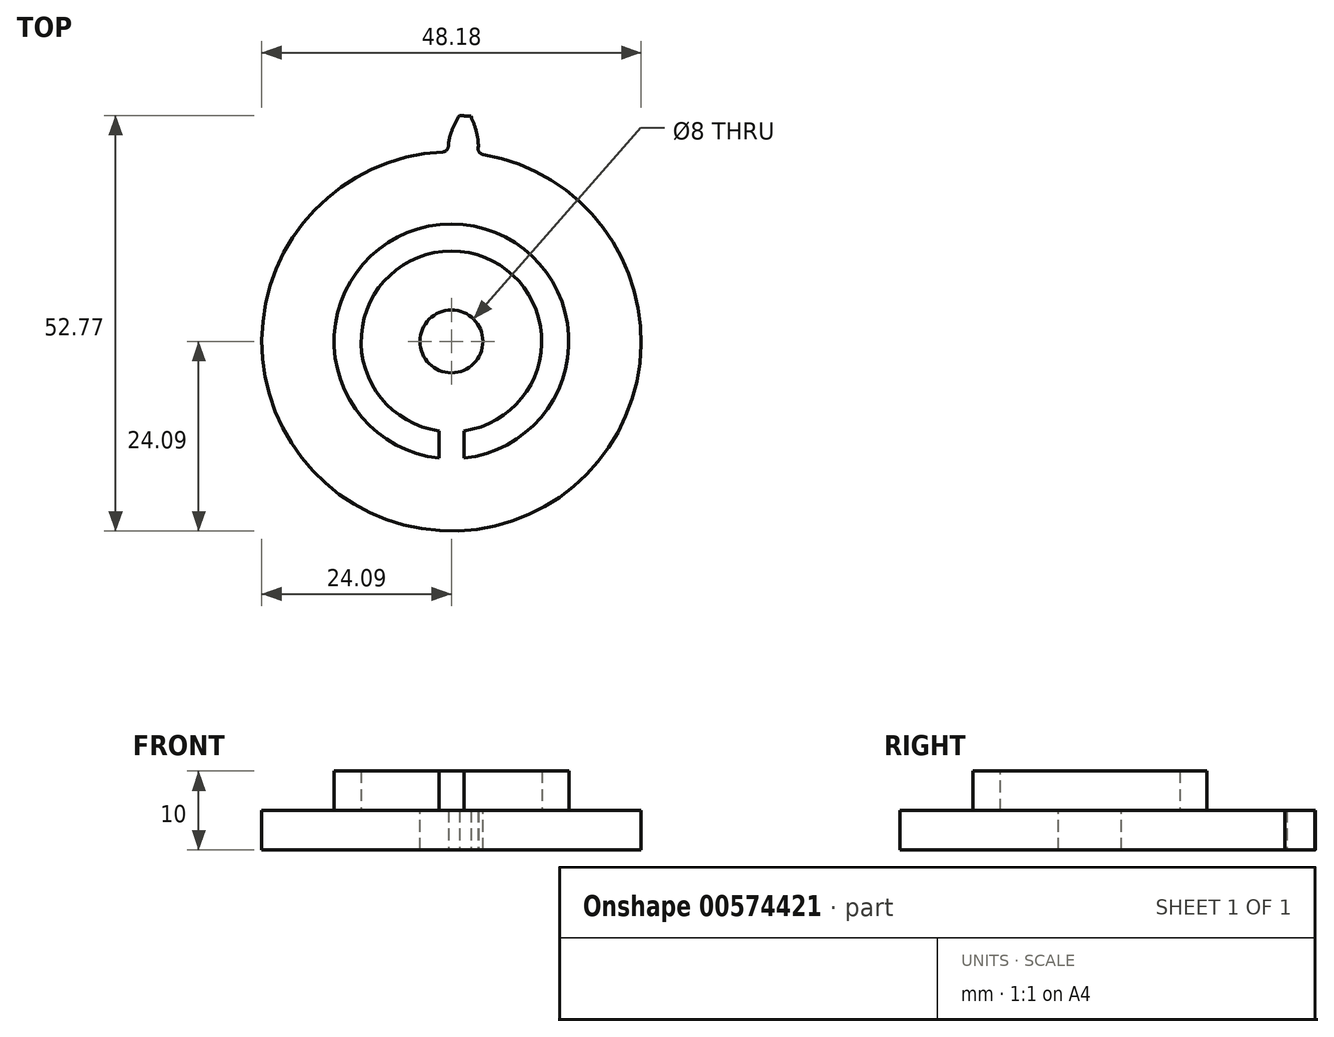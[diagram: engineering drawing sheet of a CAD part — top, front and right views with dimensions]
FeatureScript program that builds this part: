
annotation { "Feature Type Name" : "Feature", "Feature Type Description" : "" }
export const myFeature = defineFeature(function(context is Context, id is Id, definition is map)
    precondition{}
    {
        {
            var Q0;
            Q0=qCreatedBy(makeId("Front.planeOp"),FACE);
            var sketch = newSketch(context, id + "F0", { "sketchPlane" : qUnion([Q0])});
            skLineSegment(sketch, "E0", {"start": v(0, 72.27) * mm, "end": v(0, -50.25) * mm, "construction": true});
            skSolve(sketch);
        }
        {
            var Q0;
            Q0=qCreatedBy(makeId("Top.planeOp"),FACE);
            var sketch = newSketch(context, id + "F1", { "sketchPlane" : qUnion([Q0])});
            skCircle(sketch, "E1", {"center": v(0, 0) * mm, "radius": 26.65 * mm, "construction": true});
            skCircle(sketch, "E2", {"center": v(0, 0) * mm, "radius": 24.09 * mm});
            skSolve(sketch);
        }
        {
            var Q0;
            Q0=qSketchRegion(id+"F1",true);
            extrude(context, id + "F2", {"entities" : qUnion([Q0]), "depth" : 5 * mm});
        }
        {
            var Q0;
            Q0=makeQuery(id+"F2.opExtrude","CAP_FACE",FACE,{"disambiguationData":[OSD([sQuery(id+"F1.wireOp",EDGE,"E2"),sQuery(id+"F1.wireOp",EDGE,"lKhcHiEn-qWT4-b5GR-9CCX-N4hY3lJjeW35"),sQuery(id+"F1.wireOp",EDGE,"zsuhm7zz-1LAn-hH0Z-Fbhr-HMJ1RvOiH2OX")])],"isStart":false});
            var sketch = newSketch(context, id + "F3", { "sketchPlane" : qUnion([Q0])});
            skArc(sketch, "E3", {"start": v(-2.86, 2.8) * mm, "mid": v(0, -4) * mm, "end": v(2.86, 2.8) * mm});
            skPoint(sketch, "E4", {"position": v(0, 4) * mm});
            skArc(sketch, "E5", {"start": v(-2.86, 2.8) * mm, "mid": v(0, 4) * mm, "end": v(2.86, 2.8) * mm, "construction": true});
            skArc(sketch, "E6", {"start": v(-2.86, 2.8) * mm, "mid": v(1.55, -3.69) * mm, "end": v(0, 4) * mm});
            skArc(sketch, "E7", {"start": v(0, 4) * mm, "mid": v(-2.83, 2.83) * mm, "end": v(-4, 0) * mm});
            skSolve(sketch);
        }
        {
            var Q0;
            Q0=qSketchRegion(id+"F3",true);
            extrude(context, id + "F4", {"entities" : qUnion([Q0]), "operationType" : NewBodyOperationType.REMOVE, "endBound" : BoundingType.THROUGH_ALL, "oppositeDirection" : true, "depth" : 25 * mm});
        }
        {
            var Q0;
            Q0=qCreatedBy(makeId("Top.planeOp"),FACE);
            var sketch = newSketch(context, id + "F5", { "sketchPlane" : qUnion([Q0])});
            skLineSegment(sketch, "E8", {"start": v(0, 0) * mm, "end": v(0, 29.7) * mm, "construction": true});
            skLineSegment(sketch, "E9", {"start": v(0, 0) * mm, "end": v(-10.47, 28.76) * mm, "construction": true});
            skLineSegment(sketch, "E10", {"start": v(0, 26.65) * mm, "end": v(-8.57, 23.53) * mm, "construction": true});
            skCircle(sketch, "E11", {"center": v(0, 0) * mm, "radius": 26.65 * mm, "construction": true});
            skCircle(sketch, "E12", {"center": v(0, 0) * mm, "radius": 28.7 * mm, "construction": true});
            skArc(sketch, "E13", {"start": v(-1.13, 24.06) * mm, "mid": v(-1.46, -24.04) * mm, "end": v(4.02, 23.75) * mm, "construction": true});
            skCircle(sketch, "E14", {"center": v(0, 0) * mm, "radius": 25.04 * mm, "construction": true});
            skCircle(sketch, "E15", {"center": v(11, 22.5) * mm, "radius": 11.76 * mm, "construction": true});
            skCircle(sketch, "E16", {"center": v(6.53, 24.18) * mm, "radius": 6.98 * mm, "construction": true});
            skArc(sketch, "E17", {"start": v(1, 28.68) * mm, "mid": v(0.45, 27.7) * mm, "end": v(0, 26.65) * mm});
            skArc(sketch, "E18", {"start": v(0, 26.65) * mm, "mid": v(-0.25, 25.86) * mm, "end": v(-0.4, 25.04) * mm});
            skLineSegment(sketch, "E19", {"start": v(-0.4, 25.04) * mm, "end": v(-0.4, 24.84) * mm});
            skLineSegment(sketch, "E20", {"start": v(-0.38, 24.08) * mm, "end": v(0, 0) * mm, "construction": true});
            skArc(sketch, "E21", {"start": v(3.21, 26.46) * mm, "mid": v(1.61, 26.6) * mm, "end": v(0, 26.65) * mm});
            skLineSegment(sketch, "E22", {"start": v(0, 0) * mm, "end": v(1.61, 26.6) * mm, "construction": true});
            skLineSegment(sketch, "E23", {"start": v(0.78, 12.85) * mm, "end": v(1.61, 26.6) * mm, "construction": true});
            skArc(sketch, "E24", {"start": v(1.73, 28.65) * mm, "mid": v(1.37, 28.67) * mm, "end": v(1, 28.68) * mm});
            skArc(sketch, "E25.MirrorCS", {"start": v(1.73, 28.65) * mm, "mid": v(2.1, 28.62) * mm, "end": v(2.47, 28.6) * mm});
            skArc(sketch, "E26.MirrorCS", {"start": v(2.47, 28.6) * mm, "mid": v(2.9, 27.54) * mm, "end": v(3.21, 26.46) * mm});
            skArc(sketch, "E27.MirrorCS", {"start": v(3.21, 26.46) * mm, "mid": v(3.36, 25.64) * mm, "end": v(3.42, 24.8) * mm});
            skLineSegment(sketch, "E28.MirrorCS", {"start": v(3.42, 24.8) * mm, "end": v(3.39, 24.61) * mm});
            skPoint(sketch, "E29.visualSharp", {"position": v(-0.38, 24.08) * mm});
            skArc(sketch, "E29.filletArc", {"start": v(-1.13, 24.06) * mm, "mid": v(-0.6, 24.3) * mm, "end": v(-0.4, 24.84) * mm});
            skArc(sketch, "E30.MirrorCS", {"start": v(4.02, 23.75) * mm, "mid": v(3.53, 24.05) * mm, "end": v(3.39, 24.61) * mm});
            skPoint(sketch, "E31.orphan", {"position": v(3.29, 23.86) * mm});
            skArc(sketch, "E32", {"start": v(-1.13, 24.06) * mm, "mid": v(1.46, 24.04) * mm, "end": v(4.02, 23.75) * mm});
            skSolve(sketch);
        }
        {
            var Q0;
            Q0=qSketchRegion(id+"F5",true);
            extrude(context, id + "F6", {"entities" : qUnion([Q0]), "operationType" : NewBodyOperationType.ADD, "depth" : 5 * mm});
        }
        {
            var Q0;
            {var subQ0=sQuery(id+"F5.wireOp",EDGE,"E32");var subQ1=sQuery(id+"F5.wireOp",EDGE,"E30.MirrorCS");var subQ2=sQuery(id+"F5.wireOp",EDGE,"E29.filletArc");var subQ3=sQuery(id+"F5.wireOp",EDGE,"E28.MirrorCS");var subQ4=sQuery(id+"F5.wireOp",EDGE,"E27.MirrorCS");var subQ5=sQuery(id+"F5.wireOp",EDGE,"E26.MirrorCS");var subQ6=sQuery(id+"F5.wireOp",EDGE,"E25.MirrorCS");var subQ7=sQuery(id+"F5.wireOp",EDGE,"E24");var subQ8=sQuery(id+"F5.wireOp",EDGE,"E19");var subQ9=sQuery(id+"F5.wireOp",EDGE,"E18");var subQ10=sQuery(id+"F5.wireOp",EDGE,"E17");Q0=makeQuery(id+"FKo0gFQ4KOUnKrD_1.25.F6.boolean.opBoolean","MERGE",FACE,{"derivedFrom":[makeQuery(id+"FKo0gFQ4KOUnKrD_1.24.F6.boolean.opBoolean","MERGE",FACE,{"derivedFrom":[makeQuery(id+"FKo0gFQ4KOUnKrD_1.23.F6.boolean.opBoolean","MERGE",FACE,{"derivedFrom":[makeQuery(id+"FKo0gFQ4KOUnKrD_1.22.F6.boolean.opBoolean","MERGE",FACE,{"derivedFrom":[makeQuery(id+"FKo0gFQ4KOUnKrD_1.21.F6.boolean.opBoolean","MERGE",FACE,{"derivedFrom":[makeQuery(id+"FKo0gFQ4KOUnKrD_1.20.F6.boolean.opBoolean","MERGE",FACE,{"derivedFrom":[makeQuery(id+"FKo0gFQ4KOUnKrD_1.19.F6.boolean.opBoolean","MERGE",FACE,{"derivedFrom":[makeQuery(id+"FKo0gFQ4KOUnKrD_1.18.F6.boolean.opBoolean","MERGE",FACE,{"derivedFrom":[makeQuery(id+"FKo0gFQ4KOUnKrD_1.17.F6.boolean.opBoolean","MERGE",FACE,{"derivedFrom":[makeQuery(id+"FKo0gFQ4KOUnKrD_1.16.F6.boolean.opBoolean","MERGE",FACE,{"derivedFrom":[makeQuery(id+"FKo0gFQ4KOUnKrD_1.15.F6.boolean.opBoolean","MERGE",FACE,{"derivedFrom":[makeQuery(id+"FKo0gFQ4KOUnKrD_1.14.F6.boolean.opBoolean","MERGE",FACE,{"derivedFrom":[makeQuery(id+"FKo0gFQ4KOUnKrD_1.13.F6.boolean.opBoolean","MERGE",FACE,{"derivedFrom":[makeQuery(id+"FKo0gFQ4KOUnKrD_1.12.F6.boolean.opBoolean","MERGE",FACE,{"derivedFrom":[makeQuery(id+"FKo0gFQ4KOUnKrD_1.11.F6.boolean.opBoolean","MERGE",FACE,{"derivedFrom":[makeQuery(id+"FKo0gFQ4KOUnKrD_1.10.F6.boolean.opBoolean","MERGE",FACE,{"derivedFrom":[makeQuery(id+"FKo0gFQ4KOUnKrD_1.9.F6.boolean.opBoolean","MERGE",FACE,{"derivedFrom":[makeQuery(id+"FKo0gFQ4KOUnKrD_1.8.F6.boolean.opBoolean","MERGE",FACE,{"derivedFrom":[makeQuery(id+"FKo0gFQ4KOUnKrD_1.7.F6.boolean.opBoolean","MERGE",FACE,{"derivedFrom":[makeQuery(id+"FKo0gFQ4KOUnKrD_1.6.F6.boolean.opBoolean","MERGE",FACE,{"derivedFrom":[makeQuery(id+"FKo0gFQ4KOUnKrD_1.5.F6.boolean.opBoolean","MERGE",FACE,{"derivedFrom":[makeQuery(id+"FKo0gFQ4KOUnKrD_1.4.F6.boolean.opBoolean","MERGE",FACE,{"derivedFrom":[makeQuery(id+"FKo0gFQ4KOUnKrD_1.3.F6.boolean.opBoolean","MERGE",FACE,{"derivedFrom":[makeQuery(id+"FKo0gFQ4KOUnKrD_1.2.F6.boolean.opBoolean","MERGE",FACE,{"derivedFrom":[makeQuery(id+"FKo0gFQ4KOUnKrD_1.1.F6.boolean.opBoolean","MERGE",FACE,{"derivedFrom":[makeQuery(id+"F6.boolean.opBoolean","MERGE",FACE,{"derivedFrom":[makeQuery(id+"F2.opExtrude","CAP_FACE",FACE,{"disambiguationData":[OSD([sQuery(id+"F1.wireOp",EDGE,"E2")])],"isStart":false}),makeQuery(id+"F6.opExtrude","CAP_FACE",FACE,{"disambiguationData":[OSD([subQ10,subQ9,subQ8,subQ7,subQ6,subQ5,subQ4,subQ3,subQ2,subQ1,subQ0])],"isStart":false})]}),makeQuery(id+"FKo0gFQ4KOUnKrD_1.1.F6.opExtrude","CAP_FACE",FACE,{"disambiguationData":[OSD([subQ10,subQ9,subQ8,subQ7,subQ6,subQ5,subQ4,subQ3,subQ2,subQ1,subQ0])],"isStart":false})]}),makeQuery(id+"FKo0gFQ4KOUnKrD_1.2.F6.opExtrude","CAP_FACE",FACE,{"disambiguationData":[OSD([subQ10,subQ9,subQ8,subQ7,subQ6,subQ5,subQ4,subQ3,subQ2,subQ1,subQ0])],"isStart":false})]}),makeQuery(id+"FKo0gFQ4KOUnKrD_1.3.F6.opExtrude","CAP_FACE",FACE,{"disambiguationData":[OSD([subQ10,subQ9,subQ8,subQ7,subQ6,subQ5,subQ4,subQ3,subQ2,subQ1,subQ0])],"isStart":false})]}),makeQuery(id+"FKo0gFQ4KOUnKrD_1.4.F6.opExtrude","CAP_FACE",FACE,{"disambiguationData":[OSD([subQ10,subQ9,subQ8,subQ7,subQ6,subQ5,subQ4,subQ3,subQ2,subQ1,subQ0])],"isStart":false})]}),makeQuery(id+"FKo0gFQ4KOUnKrD_1.5.F6.opExtrude","CAP_FACE",FACE,{"disambiguationData":[OSD([subQ10,subQ9,subQ8,subQ7,subQ6,subQ5,subQ4,subQ3,subQ2,subQ1,subQ0])],"isStart":false})]}),makeQuery(id+"FKo0gFQ4KOUnKrD_1.6.F6.opExtrude","CAP_FACE",FACE,{"disambiguationData":[OSD([subQ10,subQ9,subQ8,subQ7,subQ6,subQ5,subQ4,subQ3,subQ2,subQ1,subQ0])],"isStart":false})]}),makeQuery(id+"FKo0gFQ4KOUnKrD_1.7.F6.opExtrude","CAP_FACE",FACE,{"disambiguationData":[OSD([subQ10,subQ9,subQ8,subQ7,subQ6,subQ5,subQ4,subQ3,subQ2,subQ1,subQ0])],"isStart":false})]}),makeQuery(id+"FKo0gFQ4KOUnKrD_1.8.F6.opExtrude","CAP_FACE",FACE,{"disambiguationData":[OSD([subQ10,subQ9,subQ8,subQ7,subQ6,subQ5,subQ4,subQ3,subQ2,subQ1,subQ0])],"isStart":false})]}),makeQuery(id+"FKo0gFQ4KOUnKrD_1.9.F6.opExtrude","CAP_FACE",FACE,{"disambiguationData":[OSD([subQ10,subQ9,subQ8,subQ7,subQ6,subQ5,subQ4,subQ3,subQ2,subQ1,subQ0])],"isStart":false})]}),makeQuery(id+"FKo0gFQ4KOUnKrD_1.10.F6.opExtrude","CAP_FACE",FACE,{"disambiguationData":[OSD([subQ10,subQ9,subQ8,subQ7,subQ6,subQ5,subQ4,subQ3,subQ2,subQ1,subQ0])],"isStart":false})]}),makeQuery(id+"FKo0gFQ4KOUnKrD_1.11.F6.opExtrude","CAP_FACE",FACE,{"disambiguationData":[OSD([subQ10,subQ9,subQ8,subQ7,subQ6,subQ5,subQ4,subQ3,subQ2,subQ1,subQ0])],"isStart":false})]}),makeQuery(id+"FKo0gFQ4KOUnKrD_1.12.F6.opExtrude","CAP_FACE",FACE,{"disambiguationData":[OSD([subQ10,subQ9,subQ8,subQ7,subQ6,subQ5,subQ4,subQ3,subQ2,subQ1,subQ0])],"isStart":false})]}),makeQuery(id+"FKo0gFQ4KOUnKrD_1.13.F6.opExtrude","CAP_FACE",FACE,{"disambiguationData":[OSD([subQ10,subQ9,subQ8,subQ7,subQ6,subQ5,subQ4,subQ3,subQ2,subQ1,subQ0])],"isStart":false})]}),makeQuery(id+"FKo0gFQ4KOUnKrD_1.14.F6.opExtrude","CAP_FACE",FACE,{"disambiguationData":[OSD([subQ10,subQ9,subQ8,subQ7,subQ6,subQ5,subQ4,subQ3,subQ2,subQ1,subQ0])],"isStart":false})]}),makeQuery(id+"FKo0gFQ4KOUnKrD_1.15.F6.opExtrude","CAP_FACE",FACE,{"disambiguationData":[OSD([subQ10,subQ9,subQ8,subQ7,subQ6,subQ5,subQ4,subQ3,subQ2,subQ1,subQ0])],"isStart":false})]}),makeQuery(id+"FKo0gFQ4KOUnKrD_1.16.F6.opExtrude","CAP_FACE",FACE,{"disambiguationData":[OSD([subQ10,subQ9,subQ8,subQ7,subQ6,subQ5,subQ4,subQ3,subQ2,subQ1,subQ0])],"isStart":false})]}),makeQuery(id+"FKo0gFQ4KOUnKrD_1.17.F6.opExtrude","CAP_FACE",FACE,{"disambiguationData":[OSD([subQ10,subQ9,subQ8,subQ7,subQ6,subQ5,subQ4,subQ3,subQ2,subQ1,subQ0])],"isStart":false})]}),makeQuery(id+"FKo0gFQ4KOUnKrD_1.18.F6.opExtrude","CAP_FACE",FACE,{"disambiguationData":[OSD([subQ10,subQ9,subQ8,subQ7,subQ6,subQ5,subQ4,subQ3,subQ2,subQ1,subQ0])],"isStart":false})]}),makeQuery(id+"FKo0gFQ4KOUnKrD_1.19.F6.opExtrude","CAP_FACE",FACE,{"disambiguationData":[OSD([subQ10,subQ9,subQ8,subQ7,subQ6,subQ5,subQ4,subQ3,subQ2,subQ1,subQ0])],"isStart":false})]}),makeQuery(id+"FKo0gFQ4KOUnKrD_1.20.F6.opExtrude","CAP_FACE",FACE,{"disambiguationData":[OSD([subQ10,subQ9,subQ8,subQ7,subQ6,subQ5,subQ4,subQ3,subQ2,subQ1,subQ0])],"isStart":false})]}),makeQuery(id+"FKo0gFQ4KOUnKrD_1.21.F6.opExtrude","CAP_FACE",FACE,{"disambiguationData":[OSD([subQ10,subQ9,subQ8,subQ7,subQ6,subQ5,subQ4,subQ3,subQ2,subQ1,subQ0])],"isStart":false})]}),makeQuery(id+"FKo0gFQ4KOUnKrD_1.22.F6.opExtrude","CAP_FACE",FACE,{"disambiguationData":[OSD([subQ10,subQ9,subQ8,subQ7,subQ6,subQ5,subQ4,subQ3,subQ2,subQ1,subQ0])],"isStart":false})]}),makeQuery(id+"FKo0gFQ4KOUnKrD_1.23.F6.opExtrude","CAP_FACE",FACE,{"disambiguationData":[OSD([subQ10,subQ9,subQ8,subQ7,subQ6,subQ5,subQ4,subQ3,subQ2,subQ1,subQ0])],"isStart":false})]}),makeQuery(id+"FKo0gFQ4KOUnKrD_1.24.F6.opExtrude","CAP_FACE",FACE,{"disambiguationData":[OSD([subQ10,subQ9,subQ8,subQ7,subQ6,subQ5,subQ4,subQ3,subQ2,subQ1,subQ0])],"isStart":false})]}),makeQuery(id+"FKo0gFQ4KOUnKrD_1.25.F6.opExtrude","CAP_FACE",FACE,{"disambiguationData":[OSD([subQ10,subQ9,subQ8,subQ7,subQ6,subQ5,subQ4,subQ3,subQ2,subQ1,subQ0])],"isStart":false})]});}
            var sketch = newSketch(context, id + "F7", { "sketchPlane" : qUnion([Q0])});
            skCircle(sketch, "E33", {"center": v(0, 0) * mm, "radius": 11.48 * mm});
            skCircle(sketch, "E34", {"center": v(0, 0) * mm, "radius": 14.9 * mm});
            skSolve(sketch);
        }
        {
            var Q0;
            Q0=makeQuery(id+"F7.imprint","IMPRINT",FACE,{"disambiguationData":[TD([[makeQuery(id+"F7.imprint","IMPRINT",EDGE,{"derivedFrom":sQuery(id+"F7.wireOp",EDGE,"E33")}),-1.0]])]});
            extrude(context, id + "F8", {"entities" : qUnion([Q0]), "operationType" : NewBodyOperationType.ADD, "depth" : 5 * mm});
        }
        {
            var Q0;
            Q0=makeQuery(id+"F8.opExtrude","CAP_FACE",FACE,{"disambiguationData":[OSD([sQuery(id+"F7.wireOp",EDGE,"E33"),sQuery(id+"F7.wireOp",EDGE,"E34")])],"isStart":false});
            var sketch = newSketch(context, id + "F9", { "sketchPlane" : qUnion([Q0])});
            skLineSegment(sketch, "E35", {"start": v(0, -11.48) * mm, "end": v(0, -14.9) * mm});
            skLineSegment(sketch, "E36", {"start": v(1.6, -11.36) * mm, "end": v(1.6, -14.82) * mm});
            skLineSegment(sketch, "E37", {"start": v(1.6, -13.1) * mm, "end": v(0, -13.1) * mm});
            skLineSegment(sketch, "E38", {"start": v(0, -13.1) * mm, "end": v(-1.6, -13.1) * mm});
            skLineSegment(sketch, "E39", {"start": v(-1.6, -13.1) * mm, "end": v(-1.6, -11.36) * mm});
            skLineSegment(sketch, "E40", {"start": v(-1.6, -13.1) * mm, "end": v(-1.6, -14.82) * mm});
            skSolve(sketch);
        }
        {
            var Q0;
            {var subQ3=sQuery(id+"F9.wireOp",EDGE,"E37");Q0=makeQuery(id+"F9.imprint","IMPRINT",FACE,{"disambiguationData":[TD([[makeQuery(id+"F9.imprint","IMPRINT",EDGE,{"derivedFrom":subQ3}),1.0]])]});}
            var Q1;
            {var subQ3=sQuery(id+"F9.wireOp",EDGE,"E37");Q1=makeQuery(id+"F9.imprint","IMPRINT",FACE,{"disambiguationData":[TD([[makeQuery(id+"F9.imprint","IMPRINT",EDGE,{"derivedFrom":subQ3}),-1.0]])]});}
            var Q2;
            {var subQ3=sQuery(id+"F9.wireOp",EDGE,"E38");Q2=makeQuery(id+"F9.imprint","IMPRINT",FACE,{"disambiguationData":[TD([[makeQuery(id+"F9.imprint","IMPRINT",EDGE,{"derivedFrom":subQ3}),1.0]])]});}
            var Q3;
            {var subQ3=sQuery(id+"F9.wireOp",EDGE,"E38");Q3=makeQuery(id+"F9.imprint","IMPRINT",FACE,{"disambiguationData":[TD([[makeQuery(id+"F9.imprint","IMPRINT",EDGE,{"derivedFrom":subQ3}),-1.0]])]});}
            extrude(context, id + "F10", {"entities" : qUnion([Q0, Q1, Q2, Q3]), "operationType" : NewBodyOperationType.REMOVE, "oppositeDirection" : true, "depth" : 5 * mm, "offsetDistance" : 25 * mm});
        }
    });
